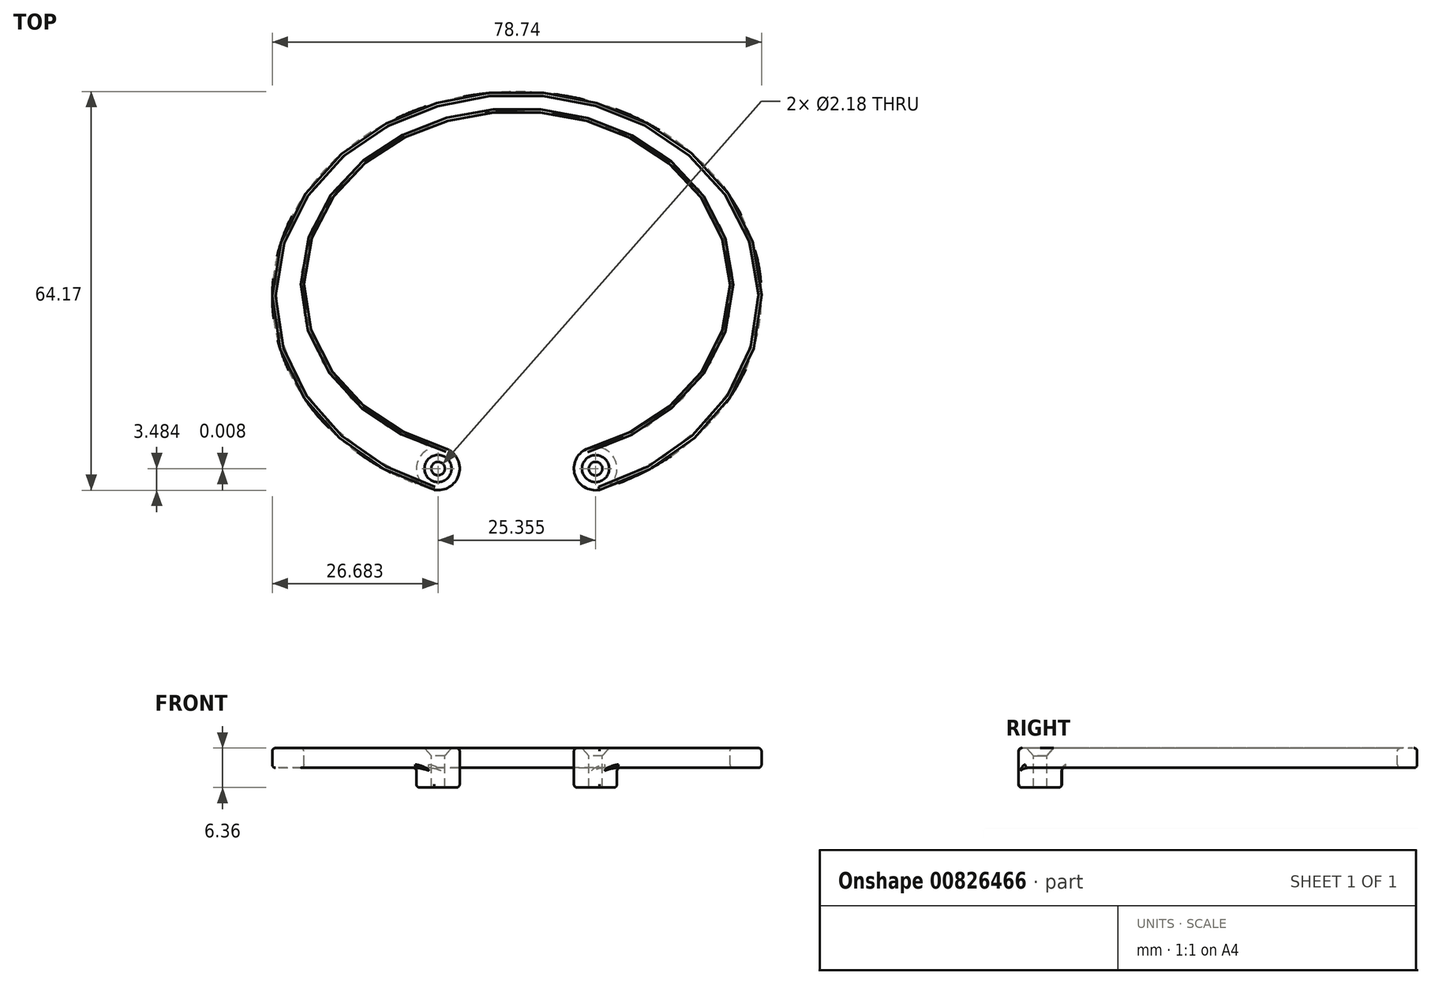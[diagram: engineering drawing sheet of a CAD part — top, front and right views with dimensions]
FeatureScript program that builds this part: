
annotation { "Feature Type Name" : "Feature", "Feature Type Description" : "" }
export const myFeature = defineFeature(function(context is Context, id is Id, definition is map)
    precondition{}
    {
        {
            var Q0;
            Q0=qCreatedBy(makeId("Top.planeOp"),FACE);
            var sketch = newSketch(context, id + "F0", { "sketchPlane" : qUnion([Q0])});
            skEllipse(sketch, "E0", {"center": v(0, 0) * mm, "majorRadius": 34.3 * mm, "minorRadius": 27.94 * mm, "majorAxis": v(1, 0)});
            skEllipse(sketch, "E1", {"center": v(0, -1.9) * mm, "majorRadius": 39.37 * mm, "minorRadius": 33.02 * mm, "majorAxis": v(1, 0)});
            skLineSegment(sketch, "E2", {"start": v(0, 0) * mm, "end": v(0, 27.94) * mm});
            skPoint(sketch, "E3", {"position": v(0, 31.12) * mm});
            skLineSegment(sketch, "E4", {"start": v(-12.7, 0) * mm, "end": v(12.7, 0) * mm});
            skLineSegment(sketch, "E5", {"start": v(-12.7, -38.35) * mm, "end": v(12.7, -38.35) * mm});
            skLineSegment(sketch, "E6", {"start": v(0, -27.94) * mm, "end": v(0, -34.93) * mm});
            skPoint(sketch, "E7", {"position": v(0, -31.43) * mm});
            skPoint(sketch, "E8", {"position": v(-36.8, 0) * mm});
            skPoint(sketch, "E9", {"position": v(36.8, 0) * mm});
            skPoint(sketch, "E10", {"position": v(0, 29.53) * mm});
            skEllipticalArc(sketch, "E11", {});
            skEllipticalArc(sketch, "E12", {});
            skLineSegment(sketch, "E13", {"start": v(0, -1.9) * mm, "end": v(-12.7, -29.63) * mm});
            skLineSegment(sketch, "E14", {"start": v(0, -1.9) * mm, "end": v(12.7, -29.63) * mm});
            skLineSegment(sketch, "E15", {"start": v(-12.7, -29.63) * mm, "end": v(-14.12, -32.73) * mm});
            skLineSegment(sketch, "E16", {"start": v(12.7, -29.63) * mm, "end": v(14.12, -32.73) * mm});
            skPoint(sketch, "E17", {"position": v(-11.22, -26.4) * mm});
            skPoint(sketch, "E18", {"position": v(11.22, -26.4) * mm});
            skArc(sketch, "E19", {"start": v(-14.12, -32.73) * mm, "mid": v(-9.52, -31) * mm, "end": v(-11.22, -26.4) * mm});
            skArc(sketch, "E20", {"start": v(11.22, -26.4) * mm, "mid": v(9.5, -31.01) * mm, "end": v(14.12, -32.73) * mm});
            skLineSegment(sketch, "E21", {"start": v(-12.7, -38.35) * mm, "end": v(-21.17, -38.35) * mm});
            skLineSegment(sketch, "E22", {"start": v(12.7, -38.35) * mm, "end": v(21.17, -38.35) * mm});
            skLineSegment(sketch, "E23", {"start": v(0, 0) * mm, "end": v(-21.17, -26.11) * mm});
            skLineSegment(sketch, "E24", {"start": v(-21.17, -26.11) * mm, "end": v(-23.18, -28.6) * mm});
            skLineSegment(sketch, "E25", {"start": v(0, 0) * mm, "end": v(21.17, -26.11) * mm});
            skLineSegment(sketch, "E26", {"start": v(21.17, -26.11) * mm, "end": v(23.18, -28.6) * mm});
            skArc(sketch, "E27", {"start": v(-11.22, -26.4) * mm, "mid": v(-15.86, -28.1) * mm, "end": v(-14.12, -32.73) * mm});
            skArc(sketch, "E28", {"start": v(14.12, -32.73) * mm, "mid": v(15.8, -28.13) * mm, "end": v(11.22, -26.4) * mm});
            const initialGuessF0  = {"E11": [0, 0, 1, 0, 0.036797212894794956, 0.029527500000000005, 0, 3.141592653589793], "E12": [0, -0.001905, 1, 0, 0.03696378320455551, 0.02952750000000001, 3.039564363503366, 0.10202829008642757]};
            skSetInitialGuess(sketch, initialGuessF0);
            skSolve(sketch);
        }
        {
            var Q0;
            {var subQ6=sQuery(id+"F0.wireOp",EDGE,"E0");var subQ7=makeQuery(id+"F0.imprint","INTERSECT",VERTEX,{"derivedFrom":[subQ6,sQuery(id+"F0.wireOp",EDGE,"E2")]});Q0=makeQuery(id+"F0.imprint","IMPRINT",FACE,{"disambiguationData":[TD([[makeQuery(id+"F0.imprint","IMPRINT",EDGE,{"disambiguationData":[TD([[subQ7,-1.0]])],"derivedFrom":subQ6}),-1.0]])]});}
            var Q1;
            {var subQ5=sQuery(id+"F0.wireOp",EDGE,"E24");Q1=makeQuery(id+"F0.imprint","IMPRINT",FACE,{"disambiguationData":[TD([[makeQuery(id+"F0.imprint","IMPRINT",EDGE,{"derivedFrom":subQ5}),-1.0]])]});}
            var Q2;
            {var subQ3=sQuery(id+"F0.wireOp",EDGE,"E24");Q2=makeQuery(id+"F0.imprint","IMPRINT",FACE,{"disambiguationData":[TD([[makeQuery(id+"F0.imprint","IMPRINT",EDGE,{"derivedFrom":subQ3}),1.0]])]});}
            var Q3;
            {var subQ0=sQuery(id+"F0.wireOp",EDGE,"E23");var subQ1=sQuery(id+"F0.wireOp",EDGE,"E0");var subQ2=makeQuery(id+"F0.imprint","INTERSECT",VERTEX,{"derivedFrom":[subQ1,subQ0]});Q3=makeQuery(id+"F0.imprint","IMPRINT",FACE,{"disambiguationData":[TD([[makeQuery(id+"F0.imprint","IMPRINT",EDGE,{"disambiguationData":[TD([[subQ2,-1.0]])],"derivedFrom":subQ1}),-1.0]])]});}
            var Q4;
            {var subQ0=sQuery(id+"F0.wireOp",EDGE,"E27");var subQ2=sQuery(id+"F0.wireOp",EDGE,"E0");var subQ4=makeQuery(id+"F0.imprint","INTERSECT",VERTEX,{"derivedFrom":[subQ2,subQ0]});Q4=makeQuery(id+"F0.imprint","IMPRINT",FACE,{"disambiguationData":[TD([[makeQuery(id+"F0.imprint","IMPRINT",EDGE,{"disambiguationData":[TD([[subQ4,-1.0]])],"derivedFrom":subQ0}),1.0]])]});}
            var Q5;
            {var subQ0=sQuery(id+"F0.wireOp",EDGE,"E15");Q5=makeQuery(id+"F0.imprint","IMPRINT",FACE,{"disambiguationData":[TD([[makeQuery(id+"F0.imprint","IMPRINT",EDGE,{"derivedFrom":subQ0}),-1.0]])]});}
            var Q6;
            {var subQ1=sQuery(id+"F0.wireOp",EDGE,"E15");Q6=makeQuery(id+"F0.imprint","IMPRINT",FACE,{"disambiguationData":[TD([[makeQuery(id+"F0.imprint","IMPRINT",EDGE,{"derivedFrom":subQ1}),1.0]])]});}
            var Q7;
            {var subQ1=sQuery(id+"F0.wireOp",EDGE,"E12");var subQ3=sQuery(id+"F0.wireOp",EDGE,"E19");var subQ4=makeQuery(id+"F0.imprint","INTERSECT",VERTEX,{"derivedFrom":[subQ1,subQ3]});Q7=makeQuery(id+"F0.imprint","IMPRINT",FACE,{"disambiguationData":[TD([[makeQuery(id+"F0.imprint","IMPRINT",EDGE,{"disambiguationData":[TD([[subQ4,1.0]])],"derivedFrom":subQ1}),1.0]])]});}
            var Q8;
            {var subQ0=sQuery(id+"F0.wireOp",EDGE,"E28");var subQ2=sQuery(id+"F0.wireOp",EDGE,"E0");var subQ4=makeQuery(id+"F0.imprint","INTERSECT",VERTEX,{"derivedFrom":[subQ2,subQ0]});Q8=makeQuery(id+"F0.imprint","IMPRINT",FACE,{"disambiguationData":[TD([[makeQuery(id+"F0.imprint","IMPRINT",EDGE,{"disambiguationData":[TD([[subQ4,1.0]])],"derivedFrom":subQ0}),1.0]])]});}
            var Q9;
            {var subQ1=sQuery(id+"F0.wireOp",EDGE,"E12");var subQ3=sQuery(id+"F0.wireOp",EDGE,"E20");var subQ4=makeQuery(id+"F0.imprint","INTERSECT",VERTEX,{"derivedFrom":[subQ1,subQ3]});Q9=makeQuery(id+"F0.imprint","IMPRINT",FACE,{"disambiguationData":[TD([[makeQuery(id+"F0.imprint","IMPRINT",EDGE,{"disambiguationData":[TD([[subQ4,-1.0]])],"derivedFrom":subQ1}),1.0]])]});}
            var Q10;
            {var subQ1=sQuery(id+"F0.wireOp",EDGE,"E16");Q10=makeQuery(id+"F0.imprint","IMPRINT",FACE,{"disambiguationData":[TD([[makeQuery(id+"F0.imprint","IMPRINT",EDGE,{"derivedFrom":subQ1}),-1.0]])]});}
            var Q11;
            {var subQ0=sQuery(id+"F0.wireOp",EDGE,"E16");Q11=makeQuery(id+"F0.imprint","IMPRINT",FACE,{"disambiguationData":[TD([[makeQuery(id+"F0.imprint","IMPRINT",EDGE,{"derivedFrom":subQ0}),1.0]])]});}
            var Q12;
            {var subQ3=sQuery(id+"F0.wireOp",EDGE,"E26");Q12=makeQuery(id+"F0.imprint","IMPRINT",FACE,{"disambiguationData":[TD([[makeQuery(id+"F0.imprint","IMPRINT",EDGE,{"derivedFrom":subQ3}),-1.0]])]});}
            var Q13;
            {var subQ0=sQuery(id+"F0.wireOp",EDGE,"E28");var subQ1=sQuery(id+"F0.wireOp",EDGE,"E0");var subQ2=makeQuery(id+"F0.imprint","INTERSECT",VERTEX,{"derivedFrom":[subQ1,subQ0]});Q13=makeQuery(id+"F0.imprint","IMPRINT",FACE,{"disambiguationData":[TD([[makeQuery(id+"F0.imprint","IMPRINT",EDGE,{"disambiguationData":[TD([[subQ2,-1.0]])],"derivedFrom":subQ1}),-1.0]])]});}
            extrude(context, id + "F1", {"entities" : qUnion([Q0, Q1, Q2, Q3, Q4, Q5, Q6, Q7, Q8, Q9, Q10, Q11, Q12, Q13]), "depth" : 3.17 * mm, "offsetDistance" : 25.4 * mm});
        }
        {
            var Q0;
            {var subQ1=sQuery(id+"F0.wireOp",EDGE,"E15");Q0=makeQuery(id+"F0.imprint","IMPRINT",FACE,{"disambiguationData":[TD([[makeQuery(id+"F0.imprint","IMPRINT",EDGE,{"derivedFrom":subQ1}),1.0]])]});}
            var Q1;
            {var subQ1=sQuery(id+"F0.wireOp",EDGE,"E12");var subQ3=sQuery(id+"F0.wireOp",EDGE,"E19");var subQ4=makeQuery(id+"F0.imprint","INTERSECT",VERTEX,{"derivedFrom":[subQ1,subQ3]});Q1=makeQuery(id+"F0.imprint","IMPRINT",FACE,{"disambiguationData":[TD([[makeQuery(id+"F0.imprint","IMPRINT",EDGE,{"disambiguationData":[TD([[subQ4,1.0]])],"derivedFrom":subQ1}),1.0]])]});}
            var Q2;
            {var subQ0=sQuery(id+"F0.wireOp",EDGE,"E27");var subQ2=sQuery(id+"F0.wireOp",EDGE,"E0");var subQ4=makeQuery(id+"F0.imprint","INTERSECT",VERTEX,{"derivedFrom":[subQ2,subQ0]});Q2=makeQuery(id+"F0.imprint","IMPRINT",FACE,{"disambiguationData":[TD([[makeQuery(id+"F0.imprint","IMPRINT",EDGE,{"disambiguationData":[TD([[subQ4,-1.0]])],"derivedFrom":subQ0}),1.0]])]});}
            var Q3;
            {var subQ0=sQuery(id+"F0.wireOp",EDGE,"E15");Q3=makeQuery(id+"F0.imprint","IMPRINT",FACE,{"disambiguationData":[TD([[makeQuery(id+"F0.imprint","IMPRINT",EDGE,{"derivedFrom":subQ0}),-1.0]])]});}
            var Q4;
            {var subQ1=sQuery(id+"F0.wireOp",EDGE,"E16");Q4=makeQuery(id+"F0.imprint","IMPRINT",FACE,{"disambiguationData":[TD([[makeQuery(id+"F0.imprint","IMPRINT",EDGE,{"derivedFrom":subQ1}),-1.0]])]});}
            var Q5;
            {var subQ0=sQuery(id+"F0.wireOp",EDGE,"E16");Q5=makeQuery(id+"F0.imprint","IMPRINT",FACE,{"disambiguationData":[TD([[makeQuery(id+"F0.imprint","IMPRINT",EDGE,{"derivedFrom":subQ0}),1.0]])]});}
            var Q6;
            {var subQ0=sQuery(id+"F0.wireOp",EDGE,"E28");var subQ2=sQuery(id+"F0.wireOp",EDGE,"E0");var subQ4=makeQuery(id+"F0.imprint","INTERSECT",VERTEX,{"derivedFrom":[subQ2,subQ0]});Q6=makeQuery(id+"F0.imprint","IMPRINT",FACE,{"disambiguationData":[TD([[makeQuery(id+"F0.imprint","IMPRINT",EDGE,{"disambiguationData":[TD([[subQ4,1.0]])],"derivedFrom":subQ0}),1.0]])]});}
            var Q7;
            {var subQ1=sQuery(id+"F0.wireOp",EDGE,"E12");var subQ3=sQuery(id+"F0.wireOp",EDGE,"E20");var subQ4=makeQuery(id+"F0.imprint","INTERSECT",VERTEX,{"derivedFrom":[subQ1,subQ3]});Q7=makeQuery(id+"F0.imprint","IMPRINT",FACE,{"disambiguationData":[TD([[makeQuery(id+"F0.imprint","IMPRINT",EDGE,{"disambiguationData":[TD([[subQ4,-1.0]])],"derivedFrom":subQ1}),1.0]])]});}
            extrude(context, id + "F2", {"entities" : qUnion([Q0, Q1, Q2, Q3, Q4, Q5, Q6, Q7]), "operationType" : NewBodyOperationType.ADD, "oppositeDirection" : true, "depth" : 3.17 * mm, "offsetDistance" : 25.4 * mm});
        }
        {
            var Q0;
            Q0=makeQuery(id+"F1.opExtrude","CAP_FACE",FACE,{"disambiguationData":[OSD([sQuery(id+"F0.wireOp",EDGE,"E0"),sQuery(id+"F0.wireOp",EDGE,"E1"),sQuery(id+"F0.wireOp",EDGE,"E19"),sQuery(id+"F0.wireOp",EDGE,"E20")])],"isStart":false});
            var sketch = newSketch(context, id + "F3", { "sketchPlane" : qUnion([Q0])});
            skPoint(sketch, "E29", {"position": v(-12.69, -29.56) * mm});
            skPoint(sketch, "E30", {"position": v(12.67, -29.57) * mm});
            skSolve(sketch);
        }
        {
            var Q0;
            {var subQ0=sQuery(id+"F0.wireOp",EDGE,"E20");var subQ1=sQuery(id+"F0.wireOp",EDGE,"E1");var subQ2=sQuery(id+"F0.wireOp",EDGE,"E19");Q0=makeQuery(id+"F2.boolean.opBoolean","MERGE",FACE,{"derivedFrom":[makeQuery(id+"F1.opExtrude","SWEPT_FACE",FACE,{"disambiguationData":[OSD([subQ1])]}),makeQuery(id+"F2.opExtrude","SWEPT_FACE",FACE,{"disambiguationData":[OSD([subQ1]),TDD([makeQuery(id+"F0.imprint","IMPRINT",EDGE,{"disambiguationData":[TD([[makeQuery(id+"F0.imprint","INTERSECT",VERTEX,{"derivedFrom":[subQ1,subQ2]}),1.0]])],"derivedFrom":subQ1})])]}),makeQuery(id+"F2.opExtrude","SWEPT_FACE",FACE,{"disambiguationData":[OSD([subQ1]),TDD([makeQuery(id+"F0.imprint","IMPRINT",EDGE,{"disambiguationData":[TD([[makeQuery(id+"F0.imprint","INTERSECT",VERTEX,{"derivedFrom":[subQ1,subQ0]}),-1.0]])],"derivedFrom":subQ1})])]})]});}
            var Q1;
            {var subQ0=sQuery(id+"F0.wireOp",EDGE,"E28");var subQ1=sQuery(id+"F0.wireOp",EDGE,"E0");var subQ2=sQuery(id+"F0.wireOp",EDGE,"E27");Q1=makeQuery(id+"F2.boolean.opBoolean","MERGE",FACE,{"derivedFrom":[makeQuery(id+"F1.opExtrude","SWEPT_FACE",FACE,{"disambiguationData":[OSD([subQ1])]}),makeQuery(id+"F2.opExtrude","SWEPT_FACE",FACE,{"disambiguationData":[OSD([subQ1]),TDD([makeQuery(id+"F0.imprint","IMPRINT",EDGE,{"disambiguationData":[TD([[makeQuery(id+"F0.imprint","INTERSECT",VERTEX,{"derivedFrom":[subQ1,subQ2]}),-1.0]])],"derivedFrom":subQ1})])]}),makeQuery(id+"F2.opExtrude","SWEPT_FACE",FACE,{"disambiguationData":[OSD([subQ1]),TDD([makeQuery(id+"F0.imprint","IMPRINT",EDGE,{"disambiguationData":[TD([[makeQuery(id+"F0.imprint","INTERSECT",VERTEX,{"derivedFrom":[subQ1,subQ0]}),1.0]])],"derivedFrom":subQ1})])]})]});}
            var Q2;
            {var subQ0=sQuery(id+"F0.wireOp",EDGE,"E20");Q2=makeQuery(id+"F2.boolean.opBoolean","MERGE",FACE,{"derivedFrom":[makeQuery(id+"F1.opExtrude","SWEPT_FACE",FACE,{"disambiguationData":[OSD([subQ0])]}),makeQuery(id+"F2.opExtrude","SWEPT_FACE",FACE,{"disambiguationData":[OSD([subQ0])]})]});}
            var Q3;
            Q3=makeQuery(id+"F2.opExtrude","SWEPT_FACE",FACE,{"disambiguationData":[OSD([sQuery(id+"F0.wireOp",EDGE,"E28")])]});
            var Q4;
            Q4=makeQuery(id+"F2.opExtrude","SWEPT_FACE",FACE,{"disambiguationData":[OSD([sQuery(id+"F0.wireOp",EDGE,"E27")])]});
            var Q5;
            {var subQ0=sQuery(id+"F0.wireOp",EDGE,"E19");Q5=makeQuery(id+"F2.boolean.opBoolean","MERGE",FACE,{"derivedFrom":[makeQuery(id+"F1.opExtrude","SWEPT_FACE",FACE,{"disambiguationData":[OSD([subQ0])]}),makeQuery(id+"F2.opExtrude","SWEPT_FACE",FACE,{"disambiguationData":[OSD([subQ0])]})]});}
            fillet(context, id + "F4", {"entities" : qUnion([Q0, Q1, Q2, Q3, Q4, Q5]), "radius" : 0.5 * mm, "tangentPropagation" : true, "allowEdgeOverflow" : false});
        }
        {
            var Q0;
            Q0=sQuery(id+"F3.wireOp",VERTEX,"E29");
            var Q1;
            Q1=sQuery(id+"F3.wireOp",VERTEX,"E30");
            var Q2;
            Q2=makeQuery(id+"F1.opExtrude","SWEPT_BODY",BODY,{"disambiguationData":[OSD([sQuery(id+"F0.wireOp",EDGE,"E0"),sQuery(id+"F0.wireOp",EDGE,"E1"),sQuery(id+"F0.wireOp",EDGE,"E19"),sQuery(id+"F0.wireOp",EDGE,"E20")])]});
            hole(context, id + "F5", {"style" : HoleStyle.C_SINK, "endStyle" : HoleEndStyle.BLIND, "holeDiameter" : 2.18 * mm, "cSinkDiameter" : 4.37 * mm, "cSinkAngle" : 82 * degree, "majorDiameter" : 1.85 * mm, "holeDepth" : 13.9 * mm, "isTappedThrough" : true, "tappedDepth" : 12.7 * mm, "tapClearance" : 3, "locations" : qUnion([Q0, Q1]), "scope" : qUnion([Q2])});
        }
    });
